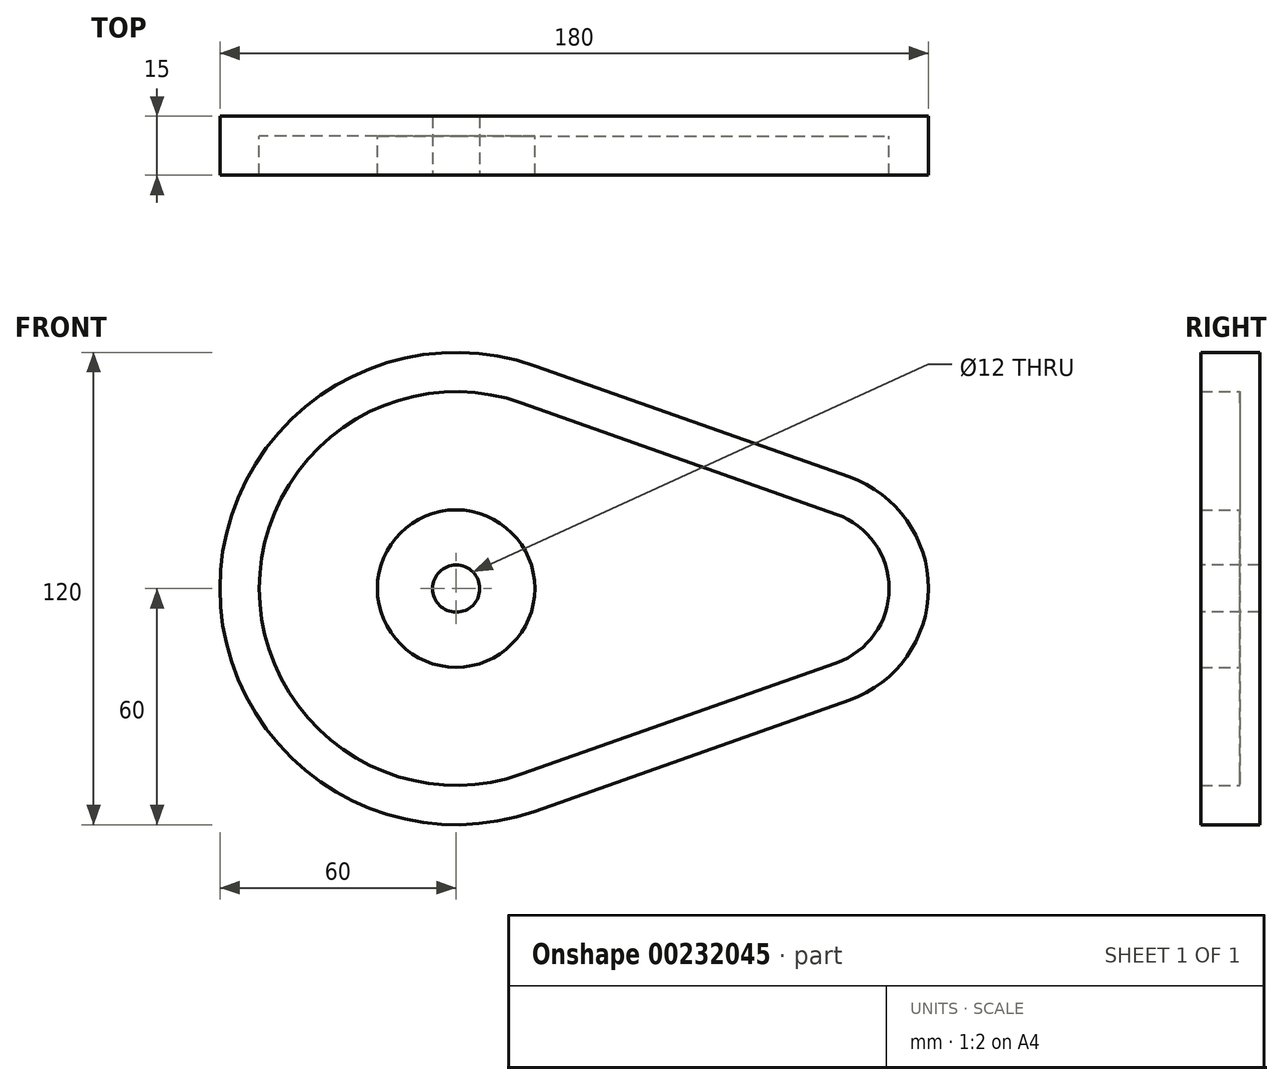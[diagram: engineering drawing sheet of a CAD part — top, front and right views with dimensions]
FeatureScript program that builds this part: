
annotation { "Feature Type Name" : "Feature", "Feature Type Description" : "" }
export const myFeature = defineFeature(function(context is Context, id is Id, definition is map)
    precondition{}
    {
        {
            var Q0;
            Q0=qCreatedBy(makeId("Front.planeOp"),FACE);
            var sketch = newSketch(context, id + "F0", { "sketchPlane" : qUnion([Q0])});
            skArc(sketch, "E0", {"start": v(-70, 56.57) * mm, "mid": v(-150, 0) * mm, "end": v(-70, -56.57) * mm});
            skArc(sketch, "E1", {"start": v(10, -28.28) * mm, "mid": v(30, 0) * mm, "end": v(10, 28.28) * mm});
            skLineSegment(sketch, "E2", {"start": v(-70, 56.57) * mm, "end": v(10, 28.28) * mm});
            skLineSegment(sketch, "E3", {"start": v(-70, -56.57) * mm, "end": v(10, -28.28) * mm});
            skLineSegment(sketch, "E4.0", {"start": v(-73.33, 47.14) * mm, "end": v(6.67, 18.86) * mm});
            skArc(sketch, "E4.1", {"start": v(-73.33, 47.14) * mm, "mid": v(-140, 0) * mm, "end": v(-73.33, -47.14) * mm});
            skLineSegment(sketch, "E4.2", {"start": v(-73.33, -47.14) * mm, "end": v(6.67, -18.86) * mm});
            skArc(sketch, "E4.3", {"start": v(6.67, -18.86) * mm, "mid": v(20, 0) * mm, "end": v(6.67, 18.86) * mm});
            skCircle(sketch, "E5", {"center": v(-90, 0) * mm, "radius": 20 * mm});
            skSolve(sketch);
        }
        {
            var Q0;
            Q0=makeQuery(id+"F0.imprint","IMPRINT",FACE,{"disambiguationData":[TD([[makeQuery(id+"F0.imprint","IMPRINT",EDGE,{"derivedFrom":sQuery(id+"F0.wireOp",EDGE,"E0")}),1.0]])]});
            var Q1;
            Q1=makeQuery(id+"F0.imprint","IMPRINT",FACE,{"disambiguationData":[TD([[makeQuery(id+"F0.imprint","IMPRINT",EDGE,{"derivedFrom":sQuery(id+"F0.wireOp",EDGE,"E5")}),1.0]])]});
            extrude(context, id + "F1", {"entities" : qUnion([Q0, Q1]), "depth" : 10 * mm});
        }
        {
            var Q0;
            Q0=makeQuery(id+"F1.opExtrude","CAP_FACE",FACE,{"disambiguationData":[OSD([sQuery(id+"F0.wireOp",EDGE,"E0"),sQuery(id+"F0.wireOp",EDGE,"E1"),sQuery(id+"F0.wireOp",EDGE,"E2"),sQuery(id+"F0.wireOp",EDGE,"E3"),sQuery(id+"F0.wireOp",EDGE,"E4.0"),sQuery(id+"F0.wireOp",EDGE,"E4.1"),sQuery(id+"F0.wireOp",EDGE,"E4.2"),sQuery(id+"F0.wireOp",EDGE,"E4.3")])],"isStart":true});
            var sketch = newSketch(context, id + "F2", { "sketchPlane" : qUnion([Q0])});
            skArc(sketch, "E6.0", {"start": v(70, 56.57) * mm, "mid": v(150, 0) * mm, "end": v(70, -56.57) * mm});
            skLineSegment(sketch, "E7.0", {"start": v(70, -56.57) * mm, "end": v(-10, -28.28) * mm});
            skArc(sketch, "E8.0", {"start": v(-10, -28.28) * mm, "mid": v(-30, 0) * mm, "end": v(-10, 28.28) * mm});
            skLineSegment(sketch, "E9.0", {"start": v(70, 56.57) * mm, "end": v(-10, 28.28) * mm});
            skSolve(sketch);
        }
        {
            var Q0;
            Q0 = qSketchRegion(id + "F2", true);
            extrude(context, id + "F3", {"entities" : qUnion([Q0]), "operationType" : NewBodyOperationType.ADD, "depth" : 5 * mm});
        }
        {
            var Q0;
            Q0=makeQuery(id+"F1.opExtrude","CAP_FACE",FACE,{"disambiguationData":[OSD([sQuery(id+"F0.wireOp",EDGE,"E5")])],"isStart":false});
            var sketch = newSketch(context, id + "F4", { "sketchPlane" : qUnion([Q0])});
            skPoint(sketch, "E10", {"position": v(-90, 0) * mm});
            skSolve(sketch);
        }
        {
            var Q0;
            Q0=sQuery(id+"F4.wireOp",VERTEX,"E10");
            var Q1;
            Q1=makeQuery(id+"F1.opExtrude","SWEPT_BODY",BODY,{"disambiguationData":[OSD([sQuery(id+"F0.wireOp",EDGE,"E0"),sQuery(id+"F0.wireOp",EDGE,"E1"),sQuery(id+"F0.wireOp",EDGE,"E2"),sQuery(id+"F0.wireOp",EDGE,"E3"),sQuery(id+"F0.wireOp",EDGE,"E4.0"),sQuery(id+"F0.wireOp",EDGE,"E4.1"),sQuery(id+"F0.wireOp",EDGE,"E4.2"),sQuery(id+"F0.wireOp",EDGE,"E4.3")])]});
            hole(context, id + "F5", {"style" : HoleStyle.SIMPLE, "endStyle" : HoleEndStyle.BLIND, "holeDiameter" : 12 * mm, "holeDepth" : 15 * mm, "locations" : qUnion([Q0]), "scope" : qUnion([Q1])});
        }
    });
